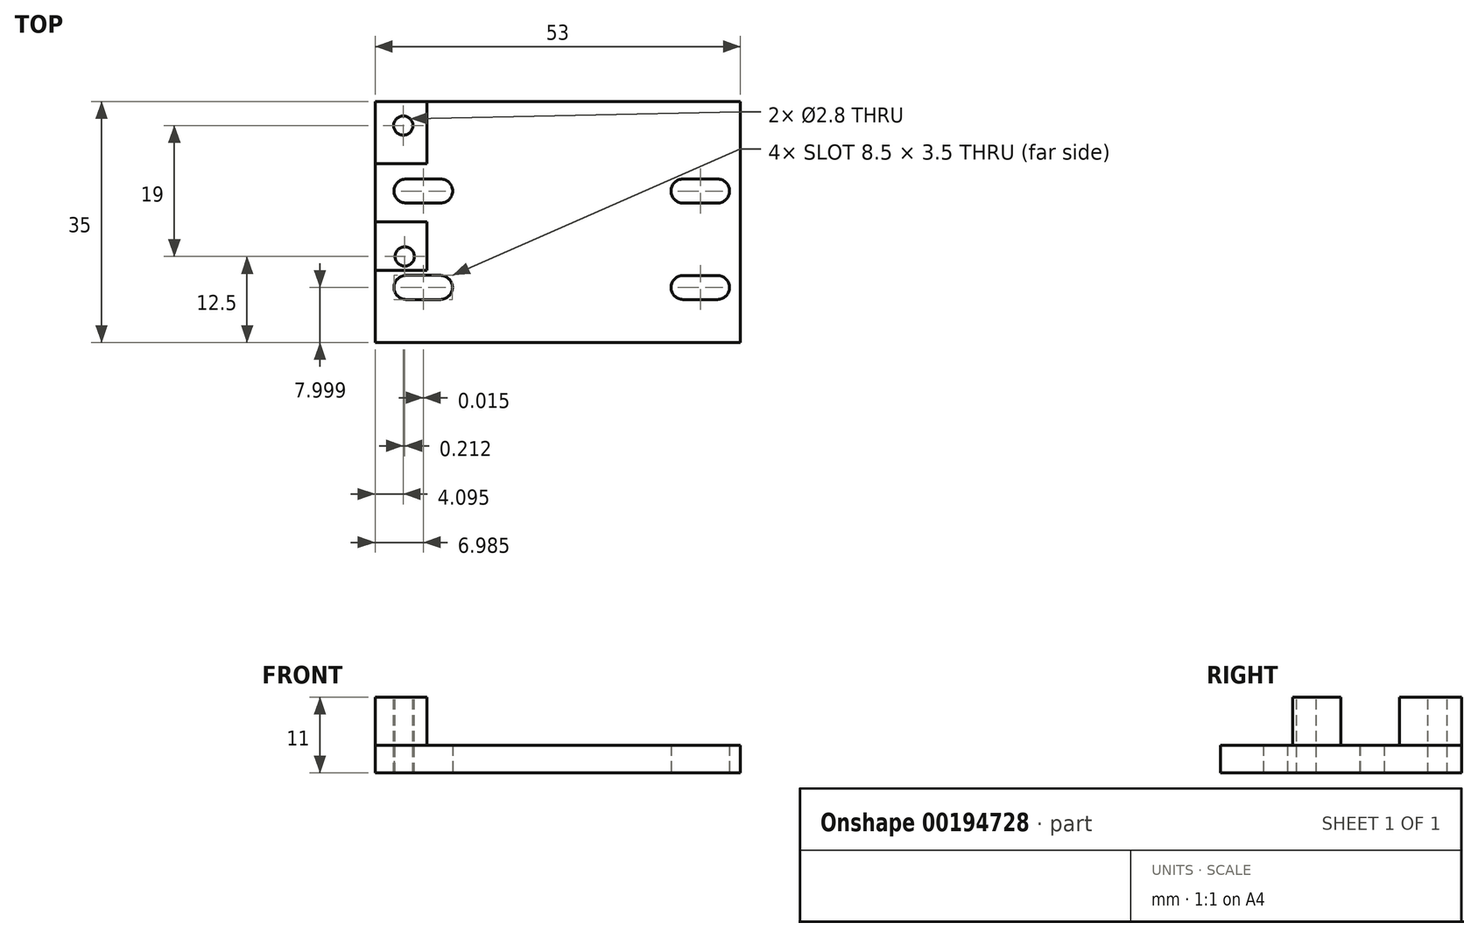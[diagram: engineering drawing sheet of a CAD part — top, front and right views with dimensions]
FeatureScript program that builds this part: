
annotation { "Feature Type Name" : "Feature", "Feature Type Description" : "" }
export const myFeature = defineFeature(function(context is Context, id is Id, definition is map)
    precondition{}
    {
        {
            var Q0;
            Q0=qCreatedBy(makeId("Top.planeOp"),FACE);
            var sketch = newSketch(context, id + "F0", { "sketchPlane" : qUnion([Q0])});
            skLineSegment(sketch, "E0", {"start": v(0, 0) * mm, "end": v(0, 35) * mm});
            skLineSegment(sketch, "E1", {"start": v(0, 35) * mm, "end": v(53, 35) * mm});
            skLineSegment(sketch, "E2", {"start": v(53, 35) * mm, "end": v(53, 0) * mm});
            skLineSegment(sketch, "E3", {"start": v(53, 0) * mm, "end": v(0, 0) * mm});
            skLineSegment(sketch, "E4", {"start": v(7, 38.4) * mm, "end": v(47, 38.4) * mm});
            skLineSegment(sketch, "E5", {"start": v(7, 38.4) * mm, "end": v(4.5, 38.4) * mm});
            skLineSegment(sketch, "E6", {"start": v(4.5, 23.75) * mm, "end": v(9.5, 23.75) * mm});
            skLineSegment(sketch, "E7", {"start": v(9.5, 20.25) * mm, "end": v(4.5, 20.25) * mm});
            skArc(sketch, "E8", {"start": v(4.5, 23.75) * mm, "mid": v(2.75, 22) * mm, "end": v(4.5, 20.25) * mm});
            skArc(sketch, "E9", {"start": v(9.5, 20.25) * mm, "mid": v(11.25, 22) * mm, "end": v(9.5, 23.75) * mm});
            skLineSegment(sketch, "E10", {"start": v(4.48, 9.75) * mm, "end": v(9.48, 9.75) * mm});
            skLineSegment(sketch, "E11", {"start": v(9.48, 6.25) * mm, "end": v(4.48, 6.25) * mm});
            skArc(sketch, "E12", {"start": v(4.48, 9.75) * mm, "mid": v(2.73, 8) * mm, "end": v(4.48, 6.25) * mm});
            skArc(sketch, "E13", {"start": v(9.48, 6.25) * mm, "mid": v(11.23, 8) * mm, "end": v(9.48, 9.75) * mm});
            skLineSegment(sketch, "E14", {"start": v(44.68, 23.75) * mm, "end": v(49.68, 23.75) * mm});
            skLineSegment(sketch, "E15", {"start": v(49.68, 20.25) * mm, "end": v(44.68, 20.25) * mm});
            skArc(sketch, "E16", {"start": v(44.68, 23.75) * mm, "mid": v(42.93, 22) * mm, "end": v(44.68, 20.25) * mm});
            skArc(sketch, "E17", {"start": v(49.68, 20.25) * mm, "mid": v(51.43, 22) * mm, "end": v(49.68, 23.75) * mm});
            skLineSegment(sketch, "E18", {"start": v(44.68, 9.74) * mm, "end": v(49.68, 9.74) * mm});
            skLineSegment(sketch, "E19", {"start": v(49.68, 6.24) * mm, "end": v(44.68, 6.24) * mm});
            skArc(sketch, "E20", {"start": v(44.68, 9.74) * mm, "mid": v(42.93, 8) * mm, "end": v(44.68, 6.24) * mm});
            skArc(sketch, "E21", {"start": v(49.68, 6.24) * mm, "mid": v(51.43, 8) * mm, "end": v(49.68, 9.74) * mm});
            skSolve(sketch);
        }
        {
            var Q0;
            Q0=makeQuery(id+"F0.imprint","IMPRINT",FACE,{"disambiguationData":[TD([[makeQuery(id+"F0.imprint","IMPRINT",EDGE,{"derivedFrom":sQuery(id+"F0.wireOp",EDGE,"E0")}),-1.0]])]});
            extrude(context, id + "F1", {"entities" : qUnion([Q0]), "depth" : 4 * mm});
        }
        {
            var Q0;
            Q0=makeQuery(id+"F1.opExtrude","CAP_FACE",FACE,{"disambiguationData":[OSD([sQuery(id+"F0.wireOp",EDGE,"E0"),sQuery(id+"F0.wireOp",EDGE,"E1"),sQuery(id+"F0.wireOp",EDGE,"E2"),sQuery(id+"F0.wireOp",EDGE,"E3"),sQuery(id+"F0.wireOp",EDGE,"E6"),sQuery(id+"F0.wireOp",EDGE,"E7"),sQuery(id+"F0.wireOp",EDGE,"E8"),sQuery(id+"F0.wireOp",EDGE,"E9"),sQuery(id+"F0.wireOp",EDGE,"E10"),sQuery(id+"F0.wireOp",EDGE,"E11"),sQuery(id+"F0.wireOp",EDGE,"E12"),sQuery(id+"F0.wireOp",EDGE,"E13"),sQuery(id+"F0.wireOp",EDGE,"E14"),sQuery(id+"F0.wireOp",EDGE,"E15"),sQuery(id+"F0.wireOp",EDGE,"E16"),sQuery(id+"F0.wireOp",EDGE,"E17"),sQuery(id+"F0.wireOp",EDGE,"E18"),sQuery(id+"F0.wireOp",EDGE,"E19"),sQuery(id+"F0.wireOp",EDGE,"E20"),sQuery(id+"F0.wireOp",EDGE,"E21")])],"isStart":false});
            var sketch = newSketch(context, id + "F2", { "sketchPlane" : qUnion([Q0])});
            skLineSegment(sketch, "E22", {"start": v(0, 35) * mm, "end": v(0, 40) * mm});
            skLineSegment(sketch, "E23", {"start": v(0, 40) * mm, "end": v(4, 40) * mm});
            skPoint(sketch, "E24.startSnap0", {"position": v(2.75, 22) * mm});
            skCircle(sketch, "E25", {"center": v(4.1, 31.5) * mm, "radius": 1.4 * mm});
            skCircle(sketch, "E26", {"center": v(4.3, 12.5) * mm, "radius": 1.4 * mm});
            skSolve(sketch);
        }
        {
            var Q0;
            Q0=makeQuery(id+"F2.imprint","IMPRINT",FACE,{"disambiguationData":[TD([[makeQuery(id+"F2.imprint","IMPRINT",EDGE,{"derivedFrom":sQuery(id+"F2.wireOp",EDGE,"E25")}),1.0]])]});
            var Q1;
            Q1=makeQuery(id+"F2.imprint","IMPRINT",FACE,{"disambiguationData":[TD([[makeQuery(id+"F2.imprint","IMPRINT",EDGE,{"derivedFrom":sQuery(id+"F2.wireOp",EDGE,"E26")}),1.0]])]});
            extrude(context, id + "F3", {"entities" : qUnion([Q0, Q1]), "operationType" : NewBodyOperationType.REMOVE, "oppositeDirection" : true, "depth" : 25 * mm});
        }
        {
            var Q0;
            Q0=makeQuery(id+"F1.opExtrude","CAP_FACE",FACE,{"disambiguationData":[OSD([sQuery(id+"F0.wireOp",EDGE,"E0"),sQuery(id+"F0.wireOp",EDGE,"E1"),sQuery(id+"F0.wireOp",EDGE,"E2"),sQuery(id+"F0.wireOp",EDGE,"E3"),sQuery(id+"F0.wireOp",EDGE,"E6"),sQuery(id+"F0.wireOp",EDGE,"E7"),sQuery(id+"F0.wireOp",EDGE,"E8"),sQuery(id+"F0.wireOp",EDGE,"E9"),sQuery(id+"F0.wireOp",EDGE,"E10"),sQuery(id+"F0.wireOp",EDGE,"E11"),sQuery(id+"F0.wireOp",EDGE,"E12"),sQuery(id+"F0.wireOp",EDGE,"E13"),sQuery(id+"F0.wireOp",EDGE,"E14"),sQuery(id+"F0.wireOp",EDGE,"E15"),sQuery(id+"F0.wireOp",EDGE,"E16"),sQuery(id+"F0.wireOp",EDGE,"E17"),sQuery(id+"F0.wireOp",EDGE,"E18"),sQuery(id+"F0.wireOp",EDGE,"E19"),sQuery(id+"F0.wireOp",EDGE,"E20"),sQuery(id+"F0.wireOp",EDGE,"E21")])],"isStart":false});
            var sketch = newSketch(context, id + "F4", { "sketchPlane" : qUnion([Q0])});
            skLineSegment(sketch, "E27", {"start": v(7.5, 35) * mm, "end": v(7.5, 26) * mm});
            skLineSegment(sketch, "E28", {"start": v(7.5, 26) * mm, "end": v(0, 26) * mm});
            skLineSegment(sketch, "E29", {"start": v(0, 26) * mm, "end": v(0, 35) * mm});
            skLineSegment(sketch, "E30", {"start": v(0, 17.5) * mm, "end": v(7.5, 17.5) * mm});
            skLineSegment(sketch, "E31", {"start": v(7.5, 17.5) * mm, "end": v(7.5, 10.5) * mm});
            skLineSegment(sketch, "E32", {"start": v(7.5, 10.5) * mm, "end": v(0, 10.5) * mm});
            skLineSegment(sketch, "E33", {"start": v(0, 10.5) * mm, "end": v(0, 17.5) * mm});
            skSolve(sketch);
        }
        {
            var Q0;
            Q0=makeQuery(id+"F4.imprint","IMPRINT",FACE,{"disambiguationData":[TD([[makeQuery(id+"F4.imprint","IMPRINT",EDGE,{"derivedFrom":sQuery(id+"F4.wireOp",EDGE,"E30")}),-1.0]])]});
            var Q1;
            {var subQ1=sQuery(id+"F4.wireOp",EDGE,"E27");Q1=makeQuery(id+"F4.imprint","IMPRINT",FACE,{"disambiguationData":[TD([[makeQuery(id+"F4.imprint","IMPRINT",EDGE,{"derivedFrom":subQ1}),-1.0]])]});}
            extrude(context, id + "F5", {"entities" : qUnion([Q0, Q1]), "operationType" : NewBodyOperationType.ADD, "depth" : 7 * mm});
        }
    });
